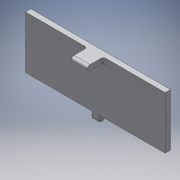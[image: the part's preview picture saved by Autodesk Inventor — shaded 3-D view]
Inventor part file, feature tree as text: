
AUTODESK INVENTOR PART (.ipt)
format: ipt  version: 2018 (Build 220112000, 112)  size: 133,120 bytes
history: native  units: in
note: dims shown in document units (in); Inventor stores cm internally (conversion verified against a paired STEP export)
features: reference x4, other x3, extrude x2, fillet x2, sketch x2
ambient origin geometry x8: Origin, YZ Plane, XZ Plane, XY Plane, X Axis, Y Axis, Z Axis, Center Point
bodies: Solid1 (feature_tree)
feature tree (13):
  extrude  "Extrusion1"  Depth=0.05in TaperAngle=0.0deg
  fillet  "Fillet1"  Radius=0.025in
  extrude  "Extrusion2"  Depth=0.025in
  fillet  "Fillet2"  Radius=0.075in
  sketch  "Sketch1"  dims[d0=0.025in d1=0.05in d2=0.0in d3=0.025in]
  reference  "Reference1"
  reference  "Reference4"
  reference  "Reference5"
  reference  "Reference6"
  sketch  "Sketch2"  dims[d4=0.05in d5=0.075in d6=0.075in d7=0.15in d8=0.0in d9=0.025in]
  other  "<userpath>\Documents\Commodore Cube Project\Case\Assembly.iam"
  other  "Assembly.iam"
  other  "Tray:1"
